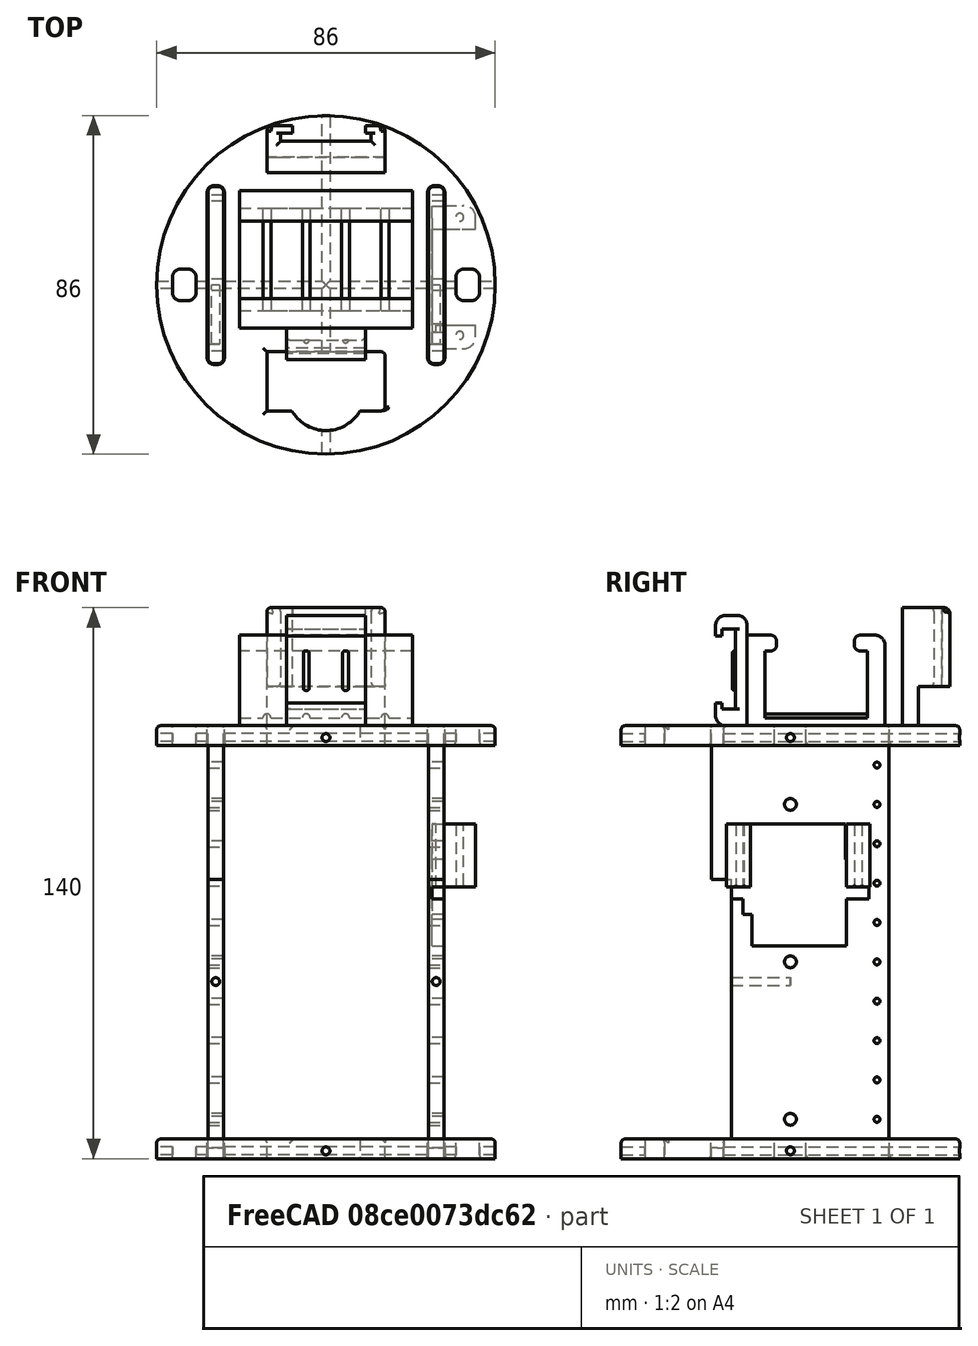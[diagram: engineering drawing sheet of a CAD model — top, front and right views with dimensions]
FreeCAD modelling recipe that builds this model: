
FCSTD DOCUMENT  (FreeCAD 0.20R29603 (Git))
Label: Capsula_Interior
License: All rights reserved
LicenseURL: http://en.wikipedia.org/wiki/All_rights_reserved
objects: Part::Cut×130, Part::Cylinder×98, Part::Fillet×96, Part::Box×72, Part::MultiFuse×37, Part::Offset×12, Part::Chamfer×1
note: 446 computed .brp shape members not serialized (recipe doc carries the construction recipe); baked Part::Feature solids carry a one-line shape summary decoded from their .brp

FEATURE [Part::Box] Box  label="Extensor"
  AttacherType = Attacher::AttachEngine3D
  Height = 66
  Length = 11
  Placement = pos=(30,-28,3) rot=(0,0,1;1.5708rad)
  Width = 60
FEATURE [Part::Box] Box001  label="Cubo001"
  AttacherType = Attacher::AttachEngine3D
  Height = 110
  Length = 45
  Placement = pos=(-30,25,0) rot=(0,0,-1;1.5708rad)
  Width = 4
FEATURE [Part::Box] Box002  label="Cubo002"
  AttacherType = Attacher::AttachEngine3D
  Height = 110
  Length = 45
  Placement = pos=(-30,25,0) rot=(0,0,-1;1.5708rad)
  Width = 4
FEATURE [Part::Box] Box003  label="Cubo003"
  AttacherType = Attacher::AttachEngine3D
  Height = 10
  Length = 30
  Placement = pos=(-15,-32,0) rot=(0,0,1;0rad)
  Width = 15
FEATURE [Part::Box] Box005  label="Cubo004"
  AttacherType = Attacher::AttachEngine3D
  Height = 15
  Length = 26
  Placement = pos=(-13,-23,110) rot=(0,0,1;0rad)
  Width = 35
FEATURE [Part::Box] Box006  label="Cubo005"
  AttacherType = Attacher::AttachEngine3D
  Height = 150
  Length = 6
  Width = 8
FEATURE [Part::Box] Box007  label="Cubo006"
  AttacherType = Attacher::AttachEngine3D
  Height = 150
  Length = 6
  Width = 8
FEATURE [Part::Box] Box008  label="Cubo007"
  AttacherType = Attacher::AttachEngine3D
  Height = 150
  Length = 6
  Width = 8
FEATURE [Part::Box] Box009  label="Cubo008"
  AttacherType = Attacher::AttachEngine3D
  Height = 150
  Length = 6
  Width = 8
FEATURE [Part::Box] Box010  label="Cubo009"
  AttacherType = Attacher::AttachEngine3D
  Height = 11.6
  Length = 20.8
  Placement = pos=(-10.5,-23,110) rot=(0,0,1;0rad)
  Width = 35
FEATURE [Part::Box] Box011  label="Cubo010"
  AttacherType = Attacher::AttachEngine3D
  Height = 11.6
  Length = 16
  Placement = pos=(-8,-23,116) rot=(0,0,1;0rad)
  Width = 35
FEATURE [Part::Box] Box095  label="Cubo095"
  AttacherType = Attacher::AttachEngine3D
  Height = 110
  Length = 45
  Placement = pos=(-30,25,0) rot=(0,0,-1;1.5708rad)
  Width = 4
FEATURE [Part::Box] Box096  label="Cubo096"
  AttacherType = Attacher::AttachEngine3D
  Height = 110
  Length = 45
  Placement = pos=(-30,25,0) rot=(0,0,-1;1.5708rad)
  Width = 4
FEATURE [Part::Box] Box097  label="Cubo097"
  AttacherType = Attacher::AttachEngine3D
  Height = 23
  Length = 24
  Width = 14
FEATURE [Part::Box] Box098  label="Cubo098"
  AttacherType = Attacher::AttachEngine3D
  Height = 3
  Length = 33.5
  Placement = pos=(-5,0,16) rot=(0,0,1;0rad)
  Width = 14
FEATURE [Part::Box] Box099  label="Cubo099"
  AttacherType = Attacher::AttachEngine3D
  Height = 1.4
  Length = 13
  Placement = pos=(9.8,5,28.6) rot=(0,0,1;0rad)
  Width = 4
FEATURE [Part::Box] Box100  label="Cubo100"
  AttacherType = Attacher::AttachEngine3D
  Height = 16
  Length = 10
  Placement = pos=(28,12.2,69) rot=(0,0,1;0rad)
  Width = 6
FEATURE [Part::Box] Box101  label="Cubo101"
  AttacherType = Attacher::AttachEngine3D
  Height = 16
  Length = 10
  Placement = pos=(28,-18.2,69) rot=(0,0,1;0rad)
  Width = 6
FEATURE [Part::Box] Box102  label="Extensor001"
  AttacherType = Attacher::AttachEngine3D
  Height = 66
  Length = 11
  Placement = pos=(30,-28,3) rot=(0,0,1;1.5708rad)
  Width = 60
FEATURE [Part::Box] Box104  label="Cubo102"
  AttacherType = Attacher::AttachEngine3D
  Height = 8
  Length = 20
  Width = 28
FEATURE [Part::Box] Box105  label="Cubo103"
  AttacherType = Attacher::AttachEngine3D
  Height = 2
  Length = 20.5
  Placement = pos=(0,4,4) rot=(0,0,1;0rad)
  Width = 20.5
FEATURE [Part::Box] Box106  label="Cubo104"
  AttacherType = Attacher::AttachEngine3D
  Height = 4
  Length = 20.5
  Placement = pos=(0,5,5) rot=(0,0,1;0rad)
  Width = 18.5
FEATURE [Part::Box] Box107  label="Cubo105"
  AttacherType = Attacher::AttachEngine3D
  Height = 8
  Length = 20
  Width = 30
FEATURE [Part::Box] Box108  label="Cubo106"
  AttacherType = Attacher::AttachEngine3D
  Height = 2
  Length = 20.5
  Placement = pos=(0,3.5,4) rot=(0,0,1;0rad)
  Width = 23
FEATURE [Part::Box] Box109  label="Cubo107"
  AttacherType = Attacher::AttachEngine3D
  Height = 4
  Length = 20.5
  Placement = pos=(0,5,5) rot=(0,0,1;0rad)
  Width = 18.5
FEATURE [Part::Box] Box110  label="Cubo108"
  AttacherType = Attacher::AttachEngine3D
  Height = 10
  Length = 20
  Placement = pos=(-9,-38,105) rot=(0,0,1;0rad)
  Width = 15
FEATURE [Part::Box] Box111  label="Cubo109"
  AttacherType = Attacher::AttachEngine3D
  Height = 110
  Length = 45
  Placement = pos=(-30,25,0) rot=(0,0,-1;1.5708rad)
  Width = 4
FEATURE [Part::Box] Box112  label="Extensor003"
  AttacherType = Attacher::AttachEngine3D
  Height = 66
  Length = 11
  Placement = pos=(30,-28,3) rot=(0,0,1;1.5708rad)
  Width = 60
FEATURE [Part::Box] Box113  label="Extensor004"
  AttacherType = Attacher::AttachEngine3D
  Height = 66
  Length = 11
  Placement = pos=(30,-28,3) rot=(0,0,1;1.5708rad)
  Width = 60
FEATURE [Part::Box] Box114  label="Cubo110"
  AttacherType = Attacher::AttachEngine3D
  Height = 110
  Length = 45
  Placement = pos=(-30,25,0) rot=(0,0,-1;1.5708rad)
  Width = 4
FEATURE [Part::Box] Box115  label="Cubo111"
  AttacherType = Attacher::AttachEngine3D
  Height = 23
  Length = 24
  Width = 14
FEATURE [Part::Box] Box116  label="Cubo112"
  AttacherType = Attacher::AttachEngine3D
  Height = 3
  Length = 33.5
  Placement = pos=(-5,0,16) rot=(0,0,1;0rad)
  Width = 14
FEATURE [Part::Box] Box117  label="Cubo113"
  AttacherType = Attacher::AttachEngine3D
  Height = 1.4
  Length = 13
  Placement = pos=(9.8,5,28.6) rot=(0,0,1;0rad)
  Width = 4
FEATURE [Part::Box] Box118  label="Cubo114"
  AttacherType = Attacher::AttachEngine3D
  Height = 16
  Length = 10
  Placement = pos=(28,12.2,69) rot=(0,0,1;0rad)
  Width = 6
FEATURE [Part::Box] Box119  label="Cubo115"
  AttacherType = Attacher::AttachEngine3D
  Height = 16
  Length = 10
  Placement = pos=(28,-18.2,69) rot=(0,0,1;0rad)
  Width = 6
FEATURE [Part::Box] Box120  label="Cubo116"
  AttacherType = Attacher::AttachEngine3D
  Height = 10
  Length = 4
  Placement = pos=(-30,-20,0) rot=(0,0,1;0rad)
  Width = 45
FEATURE [Part::Box] Box121  label="Cubo117"
  AttacherType = Attacher::AttachEngine3D
  Height = 10
  Length = 4
  Placement = pos=(-30,-20,0) rot=(0,0,1;0rad)
  Width = 45
FEATURE [Part::Box] Box122  label="Cubo118"
  AttacherType = Attacher::AttachEngine3D
  Height = 8
  Length = 20
  Width = 30
FEATURE [Part::Box] Box123  label="Cubo119"
  AttacherType = Attacher::AttachEngine3D
  Height = 2
  Length = 20.5
  Placement = pos=(0,3.5,4) rot=(0,0,1;0rad)
  Width = 23
FEATURE [Part::Box] Box124  label="Cubo120"
  AttacherType = Attacher::AttachEngine3D
  Height = 4
  Length = 20.5
  Placement = pos=(0,5,5) rot=(0,0,1;0rad)
  Width = 18.5
FEATURE [Part::Box] Box128  label="Cubo124"
  AttacherType = Attacher::AttachEngine3D
  Height = 30
  Length = 33
  Placement = pos=(-16,-43,115) rot=(0,0,1;0rad)
  Width = 30
FEATURE [Part::Box] Box129  label="Cubo125"
  AttacherType = Attacher::AttachEngine3D
  Height = 30
  Length = 33
  Placement = pos=(-16,13,110) rot=(0,0,1;0rad)
  Width = 30
FEATURE [Part::Box] Box130  label="Cubo126"
  AttacherType = Attacher::AttachEngine3D
  Height = 30
  Length = 30
  Placement = pos=(-16,13,110) rot=(0,0,1;0rad)
  Width = 4
FEATURE [Part::Box] Box131  label="Cubo127"
  AttacherType = Attacher::AttachEngine3D
  Height = 3.4
  Length = 21
  Placement = pos=(0,4.2,3) rot=(0,0,1;0rad)
  Width = 20.4
FEATURE [Part::Box] Box132  label="Cubo128"
  AttacherType = Attacher::AttachEngine3D
  Height = 4
  Length = 21
  Placement = pos=(0,5.75,6) rot=(0,0,1;0rad)
  Width = 17
FEATURE [Part::Box] Box133  label="Cubo129"
  AttacherType = Attacher::AttachEngine3D
  Height = 8
  Length = 20
  Width = 28
FEATURE [Part::Box] Box134  label="Cubo130"
  AttacherType = Attacher::AttachEngine3D
  Height = 16
  Length = 37
  Placement = pos=(-19,-15,110) rot=(0,0,1;0rad)
  Width = 30
FEATURE [Part::Box] Box135  label="Pila_ext"
  AttacherType = Attacher::AttachEngine3D
  Height = 25
  Length = 44
  Placement = pos=(-22,-11,110) rot=(0,0,1;0rad)
  Width = 35
FEATURE [Part::Box] Box136  label="Pila_int"
  AttacherType = Attacher::AttachEngine3D
  Height = 17
  Length = 44
  Placement = pos=(-22,-6.5,114) rot=(0,0,1;0rad)
  Width = 26
FEATURE [Part::Box] Box137  label="hueco_pila"
  AttacherType = Attacher::AttachEngine3D
  Height = 16.65
  Length = 44
  Placement = pos=(-22,-3.5,122) rot=(0,0,1;0rad)
  Width = 19.72
FEATURE [Part::Box] Box165  label="Cubo155"
  AttacherType = Attacher::AttachEngine3D
  Height = 17
  Length = 19
  Placement = pos=(27,-9.8,59) rot=(0,0,1;0rad)
  Width = 24
FEATURE [Part::Box] Box166  label="Cubo156"
  AttacherType = Attacher::AttachEngine3D
  Height = 66
  Length = 60
  Placement = pos=(-30,-20,5) rot=(0,0,1;0rad)
  Width = 5
FEATURE [Part::Box] Box167  label="Cubo157"
  AttacherType = Attacher::AttachEngine3D
  Height = 66
  Length = 60
  Placement = pos=(-30,-20,5) rot=(0,0,1;0rad)
  Width = 5
FEATURE [Part::Box] Box168  label="Cubo158"
  AttacherType = Attacher::AttachEngine3D
  Height = 3
  Length = 4
  Placement = pos=(27,7,66) rot=(0,0,1;0rad)
  Width = 13
FEATURE [Part::Box] Box169  label="Cubo159"
  AttacherType = Attacher::AttachEngine3D
  Height = 3
  Length = 4
  Placement = pos=(27,-9.8,56) rot=(0,0,1;0rad)
  Width = 24
FEATURE [Part::Box] Box170  label="Cubo160"
  AttacherType = Attacher::AttachEngine3D
  Height = 10
  Length = 30
  Placement = pos=(-15,-32,0) rot=(0,0,1;0rad)
  Width = 15
FEATURE [Part::Box] Box171  label="Cubo161"
  AttacherType = Attacher::AttachEngine3D
  Height = 150
  Length = 6
  Width = 8
FEATURE [Part::Box] Box172  label="Cubo162"
  AttacherType = Attacher::AttachEngine3D
  Height = 150
  Length = 6
  Width = 8
FEATURE [Part::Box] Box173  label="Cubo163"
  AttacherType = Attacher::AttachEngine3D
  Height = 110
  Length = 45
  Placement = pos=(-30,25,0) rot=(0,0,-1;1.5708rad)
  Width = 4
FEATURE [Part::Box] Box174  label="Extensor005"
  AttacherType = Attacher::AttachEngine3D
  Height = 66
  Length = 11
  Placement = pos=(30,-28,3) rot=(0,0,1;1.5708rad)
  Width = 60
FEATURE [Part::Box] Box175  label="Extensor006"
  AttacherType = Attacher::AttachEngine3D
  Height = 66
  Length = 11
  Placement = pos=(30,-28,3) rot=(0,0,1;1.5708rad)
  Width = 60
FEATURE [Part::Box] Box176  label="Cubo164"
  AttacherType = Attacher::AttachEngine3D
  Height = 110
  Length = 45
  Placement = pos=(-30,25,0) rot=(0,0,-1;1.5708rad)
  Width = 4
FEATURE [Part::Box] Box177  label="Cubo165"
  AttacherType = Attacher::AttachEngine3D
  Height = 23
  Length = 24
  Width = 14
FEATURE [Part::Box] Box178  label="Cubo166"
  AttacherType = Attacher::AttachEngine3D
  Height = 3
  Length = 33.5
  Placement = pos=(-5,0,16) rot=(0,0,1;0rad)
  Width = 14
FEATURE [Part::Box] Box179  label="Cubo167"
  AttacherType = Attacher::AttachEngine3D
  Height = 1.4
  Length = 13
  Placement = pos=(9.8,5,28.6) rot=(0,0,1;0rad)
  Width = 4
FEATURE [Part::Box] Box180  label="Cubo168"
  AttacherType = Attacher::AttachEngine3D
  Height = 16
  Length = 10
  Placement = pos=(28,12.2,69) rot=(0,0,1;0rad)
  Width = 6
FEATURE [Part::Box] Box181  label="Cubo169"
  AttacherType = Attacher::AttachEngine3D
  Height = 16
  Length = 10
  Placement = pos=(28,-18.2,69) rot=(0,0,1;0rad)
  Width = 6
FEATURE [Part::Box] Box182  label="Cubo170"
  AttacherType = Attacher::AttachEngine3D
  Height = 10
  Length = 4
  Placement = pos=(-30,-20,0) rot=(0,0,1;0rad)
  Width = 45
FEATURE [Part::Box] Box183  label="Cubo171"
  AttacherType = Attacher::AttachEngine3D
  Height = 10
  Length = 4
  Placement = pos=(-30,-20,0) rot=(0,0,1;0rad)
  Width = 45
FEATURE [Part::Box] Box184  label="Cubo172"
  AttacherType = Attacher::AttachEngine3D
  Height = 10
  Length = 120
  Placement = pos=(-50,-47,100) rot=(0,0,1;0rad)
  Width = 120
FEATURE [Part::Box] Box197  label="Cubo184"
  AttacherType = Attacher::AttachEngine3D
  Height = 16
  Length = 3
  Placement = pos=(27,12,69) rot=(0,0,1;0rad)
  Width = 2
FEATURE [Part::Box] Box198  label="Cubo185"
  AttacherType = Attacher::AttachEngine3D
  Height = 24
  Length = 3
  Placement = pos=(27,14.2,54) rot=(1,0,0;1.5708rad)
  Width = 4
FEATURE [Part::Cut] Cut016
  Base = -> Box005
  Tool = -> Box010
FEATURE [Part::Cut] Cut017
  Base = -> Cut016
  Placement = pos=(-5,0,0) rot=(0,0,1;1.5708rad)
  Tool = -> Box011
FEATURE [Part::Cut] Cut115
  Base = -> Box104
  Tool = -> Box105
FEATURE [Part::Cut] Cut116
  Base = -> Cut115
  Tool = -> Box106
FEATURE [Part::Cut] Cut117
  Base = -> Box107
  Tool = -> Box108
FEATURE [Part::Cut] Cut118
  Base = -> Cut117
  Tool = -> Box109
FEATURE [Part::Cut] Cut143
  Base = -> Box122
  Tool = -> Box123
FEATURE [Part::Cut] Cut144
  Base = -> Cut143
  Tool = -> Box124
FEATURE [Part::Cut] Cut149
  Base = -> Box133
  Tool = -> Box131
FEATURE [Part::Cut] Cut150
  Base = -> Cut149
  Tool = -> Box132
FEATURE [Part::Cut] Cut152
  Base = -> Box135
  Tool = -> Box136
FEATURE [Part::Cut] Cut153  label="PortaPIlas_9V"
  Base = -> Cut152
  Placement = pos=(0,0,-2) rot=(0,0,1;0rad)
  Tool = -> Box137
FEATURE [Part::Cylinder] Cylinder  label="Cilindro"
  Angle = 360
  AttacherType = Attacher::AttachEngine3D
  FirstAngle = 0
  Height = 5
  Radius = 43
  SecondAngle = 0
FEATURE [Part::Cylinder] Cylinder002  label="Cilindro002"
  Angle = 360
  AttacherType = Attacher::AttachEngine3D
  FirstAngle = 0
  Height = 20
  Placement = pos=(0,44,1.5) rot=(1,0,0;1.5708rad)
  Radius = 0.5
  SecondAngle = 0
FEATURE [Part::Cylinder] Cylinder003  label="Cilindro003"
  Angle = 360
  AttacherType = Attacher::AttachEngine3D
  FirstAngle = 0
  Height = 20
  Placement = pos=(0,-26,1.5) rot=(1,0,0;1.5708rad)
  Radius = 0.5
  SecondAngle = 0
FEATURE [Part::Cylinder] Cylinder004  label="Cilindro004"
  Angle = 360
  AttacherType = Attacher::AttachEngine3D
  FirstAngle = 0
  Height = 3
  Radius = 43
  SecondAngle = 0
FEATURE [Part::Cylinder] Cylinder005  label="Cilindro005"
  Angle = 360
  AttacherType = Attacher::AttachEngine3D
  FirstAngle = 0
  Height = 20
  Placement = pos=(0,44,1.5) rot=(1,0,0;1.5708rad)
  Radius = 0.5
  SecondAngle = 0
FEATURE [Part::Cylinder] Cylinder006  label="Cilindro006"
  Angle = 360
  AttacherType = Attacher::AttachEngine3D
  FirstAngle = 0
  Height = 20
  Placement = pos=(0,-26,1.5) rot=(1,0,0;1.5708rad)
  Radius = 0.5
  SecondAngle = 0
FEATURE [Part::Cylinder] Cylinder008  label="Cilindro008"
  Angle = 360
  AttacherType = Attacher::AttachEngine3D
  FirstAngle = 0
  Height = 100
  Placement = pos=(-46,0,50) rot=(0,1,0;1.5708rad)
  Radius = 1.5
  SecondAngle = 0
FEATURE [Part::Cylinder] Cylinder009  label="Cilindro009"
  Angle = 360
  AttacherType = Attacher::AttachEngine3D
  FirstAngle = 0
  Height = 100
  Placement = pos=(-46,0,90) rot=(0,1,0;1.5708rad)
  Radius = 1.5
  SecondAngle = 0
FEATURE [Part::Cylinder] Cylinder010  label="Cilindro010"
  Angle = 360
  AttacherType = Attacher::AttachEngine3D
  FirstAngle = 0
  Height = 100
  Placement = pos=(-46,0,10) rot=(0,1,0;1.5708rad)
  Radius = 1.5
  SecondAngle = 0
FEATURE [Part::Cylinder] Cylinder011  label="Cilindro011"
  Angle = 360
  AttacherType = Attacher::AttachEngine3D
  FirstAngle = 0
  Height = 10
  Placement = pos=(0,-27,0) rot=(0,0,1;0rad)
  Radius = 10
  SecondAngle = 0
FEATURE [Part::Cylinder] Cylinder071  label="Cilindro071"
  Angle = 360
  AttacherType = Attacher::AttachEngine3D
  FirstAngle = 0
  Height = 100
  Placement = pos=(-46,0,50) rot=(0,1,0;1.5708rad)
  Radius = 1.5
  SecondAngle = 0
FEATURE [Part::Cylinder] Cylinder072  label="Cilindro072"
  Angle = 360
  AttacherType = Attacher::AttachEngine3D
  FirstAngle = 0
  Height = 100
  Placement = pos=(-46,0,90) rot=(0,1,0;1.5708rad)
  Radius = 1.5
  SecondAngle = 0
FEATURE [Part::Cylinder] Cylinder073  label="Cilindro073"
  Angle = 360
  AttacherType = Attacher::AttachEngine3D
  FirstAngle = 0
  Height = 100
  Placement = pos=(-46,0,10) rot=(0,1,0;1.5708rad)
  Radius = 1.5
  SecondAngle = 0
FEATURE [Part::Cylinder] Cylinder074  label="Cilindro074"
  Angle = 360
  AttacherType = Attacher::AttachEngine3D
  FirstAngle = 0
  Height = 3
  Placement = pos=(7,7,23) rot=(0,0,1;0rad)
  Radius = 7
  SecondAngle = 0
FEATURE [Part::Cylinder] Cylinder075  label="Cilindro075"
  Angle = 360
  AttacherType = Attacher::AttachEngine3D
  FirstAngle = 0
  Height = 3
  Placement = pos=(14,7,23) rot=(0,0,1;0rad)
  Radius = 2
  SecondAngle = 0
FEATURE [Part::Cylinder] Cylinder076  label="Cilindro076"
  Angle = 360
  AttacherType = Attacher::AttachEngine3D
  FirstAngle = 0
  Height = 10
  Placement = pos=(-3.2,7,12) rot=(0,0,1;0rad)
  Radius = 1.65
  SecondAngle = 0
FEATURE [Part::Cylinder] Cylinder077  label="Cilindro077"
  Angle = 360
  AttacherType = Attacher::AttachEngine3D
  FirstAngle = 0
  Height = 10
  Placement = pos=(26.8,7,12) rot=(0,0,1;0rad)
  Radius = 1.65
  SecondAngle = 0
FEATURE [Part::Cylinder] Cylinder078  label="Cilindro078"
  Angle = 360
  AttacherType = Attacher::AttachEngine3D
  FirstAngle = 0
  Height = 4
  Placement = pos=(7,7,26) rot=(0,0,1;0rad)
  Radius = 3.5
  SecondAngle = 0
FEATURE [Part::Cylinder] Cylinder079  label="Cilindro079"
  Angle = 360
  AttacherType = Attacher::AttachEngine3D
  FirstAngle = 0
  Height = 10
  Placement = pos=(21,7,25) rot=(0,0,1;0rad)
  Radius = 0.25
  SecondAngle = 0
FEATURE [Part::Cylinder] Cylinder080  label="Cilindro080"
  Angle = 360
  AttacherType = Attacher::AttachEngine3D
  FirstAngle = 0
  Height = 10
  Placement = pos=(19,7,25) rot=(0,0,1;0rad)
  Radius = 0.25
  SecondAngle = 0
FEATURE [Part::Cylinder] Cylinder081  label="Cilindro081"
  Angle = 360
  AttacherType = Attacher::AttachEngine3D
  FirstAngle = 0
  Height = 10
  Placement = pos=(17,7,25) rot=(0,0,1;0rad)
  Radius = 0.25
  SecondAngle = 0
FEATURE [Part::Cylinder] Cylinder082  label="Cilindro082"
  Angle = 360
  AttacherType = Attacher::AttachEngine3D
  FirstAngle = 0
  Height = 10
  Placement = pos=(15,7,27) rot=(0,0,1;0rad)
  Radius = 0.25
  SecondAngle = 0
FEATURE [Part::Cylinder] Cylinder083  label="Cilindro083"
  Angle = 360
  AttacherType = Attacher::AttachEngine3D
  FirstAngle = 0
  Height = 10
  Placement = pos=(13,7,27) rot=(0,0,1;0rad)
  Radius = 0.25
  SecondAngle = 0
FEATURE [Part::Cylinder] Cylinder084  label="Cilindro084"
  Angle = 360
  AttacherType = Attacher::AttachEngine3D
  FirstAngle = 0
  Height = 20
  Placement = pos=(34,-14.8,66) rot=(0,0,1;0rad)
  Radius = 1
  SecondAngle = 0
FEATURE [Part::Cylinder] Cylinder085  label="Cilindro085"
  Angle = 360
  AttacherType = Attacher::AttachEngine3D
  FirstAngle = 0
  Height = 20
  Placement = pos=(34,15.2,66) rot=(0,0,1;0rad)
  Radius = 1
  SecondAngle = 0
FEATURE [Part::Cylinder] Cylinder086  label="Cilindro086"
  Angle = 360
  AttacherType = Attacher::AttachEngine3D
  FirstAngle = 0
  Height = 100
  Placement = pos=(-46,0,50) rot=(0,1,0;1.5708rad)
  Radius = 1.5
  SecondAngle = 0
FEATURE [Part::Cylinder] Cylinder087  label="Cilindro087"
  Angle = 360
  AttacherType = Attacher::AttachEngine3D
  FirstAngle = 0
  Height = 100
  Placement = pos=(-46,0,90) rot=(0,1,0;1.5708rad)
  Radius = 1.5
  SecondAngle = 0
FEATURE [Part::Cylinder] Cylinder088  label="Cilindro088"
  Angle = 360
  AttacherType = Attacher::AttachEngine3D
  FirstAngle = 0
  Height = 100
  Placement = pos=(-46,0,10) rot=(0,1,0;1.5708rad)
  Radius = 1.5
  SecondAngle = 0
FEATURE [Part::Cylinder] Cylinder089  label="Cilindro089"
  Angle = 360
  AttacherType = Attacher::AttachEngine3D
  FirstAngle = 0
  Height = 100
  Placement = pos=(-46,0,50) rot=(0,1,0;1.5708rad)
  Radius = 1.5
  SecondAngle = 0
FEATURE [Part::Cylinder] Cylinder090  label="Cilindro090"
  Angle = 360
  AttacherType = Attacher::AttachEngine3D
  FirstAngle = 0
  Height = 100
  Placement = pos=(-46,0,90) rot=(0,1,0;1.5708rad)
  Radius = 1.5
  SecondAngle = 0
FEATURE [Part::Cylinder] Cylinder091  label="Cilindro091"
  Angle = 360
  AttacherType = Attacher::AttachEngine3D
  FirstAngle = 0
  Height = 100
  Placement = pos=(-46,0,10) rot=(0,1,0;1.5708rad)
  Radius = 1.5
  SecondAngle = 0
FEATURE [Part::Cylinder] Cylinder092  label="Cilindro092"
  Angle = 360
  AttacherType = Attacher::AttachEngine3D
  FirstAngle = 0
  Height = 3
  Placement = pos=(7,7,23) rot=(0,0,1;0rad)
  Radius = 7
  SecondAngle = 0
FEATURE [Part::Cylinder] Cylinder093  label="Cilindro093"
  Angle = 360
  AttacherType = Attacher::AttachEngine3D
  FirstAngle = 0
  Height = 3
  Placement = pos=(14,7,23) rot=(0,0,1;0rad)
  Radius = 2
  SecondAngle = 0
FEATURE [Part::Cylinder] Cylinder094  label="Cilindro094"
  Angle = 360
  AttacherType = Attacher::AttachEngine3D
  FirstAngle = 0
  Height = 10
  Placement = pos=(-3.2,7,12) rot=(0,0,1;0rad)
  Radius = 1.65
  SecondAngle = 0
FEATURE [Part::Cylinder] Cylinder095  label="Cilindro095"
  Angle = 360
  AttacherType = Attacher::AttachEngine3D
  FirstAngle = 0
  Height = 10
  Placement = pos=(26.8,7,12) rot=(0,0,1;0rad)
  Radius = 1.65
  SecondAngle = 0
FEATURE [Part::Cylinder] Cylinder096  label="Cilindro096"
  Angle = 360
  AttacherType = Attacher::AttachEngine3D
  FirstAngle = 0
  Height = 4
  Placement = pos=(7,7,26) rot=(0,0,1;0rad)
  Radius = 3.5
  SecondAngle = 0
FEATURE [Part::Cylinder] Cylinder097  label="Cilindro097"
  Angle = 360
  AttacherType = Attacher::AttachEngine3D
  FirstAngle = 0
  Height = 10
  Placement = pos=(21,7,25) rot=(0,0,1;0rad)
  Radius = 0.25
  SecondAngle = 0
FEATURE [Part::Cylinder] Cylinder098  label="Cilindro098"
  Angle = 360
  AttacherType = Attacher::AttachEngine3D
  FirstAngle = 0
  Height = 10
  Placement = pos=(19,7,25) rot=(0,0,1;0rad)
  Radius = 0.25
  SecondAngle = 0
FEATURE [Part::Cylinder] Cylinder099  label="Cilindro099"
  Angle = 360
  AttacherType = Attacher::AttachEngine3D
  FirstAngle = 0
  Height = 10
  Placement = pos=(17,7,25) rot=(0,0,1;0rad)
  Radius = 0.25
  SecondAngle = 0
FEATURE [Part::Cylinder] Cylinder100  label="Cilindro100"
  Angle = 360
  AttacherType = Attacher::AttachEngine3D
  FirstAngle = 0
  Height = 10
  Placement = pos=(15,7,27) rot=(0,0,1;0rad)
  Radius = 0.25
  SecondAngle = 0
FEATURE [Part::Cylinder] Cylinder101  label="Cilindro101"
  Angle = 360
  AttacherType = Attacher::AttachEngine3D
  FirstAngle = 0
  Height = 10
  Placement = pos=(13,7,27) rot=(0,0,1;0rad)
  Radius = 0.25
  SecondAngle = 0
FEATURE [Part::Cylinder] Cylinder102  label="Cilindro102"
  Angle = 360
  AttacherType = Attacher::AttachEngine3D
  FirstAngle = 0
  Height = 20
  Placement = pos=(34,-14.8,66) rot=(0,0,1;0rad)
  Radius = 1
  SecondAngle = 0
FEATURE [Part::Cylinder] Cylinder103  label="Cilindro103"
  Angle = 360
  AttacherType = Attacher::AttachEngine3D
  FirstAngle = 0
  Height = 20
  Placement = pos=(34,15.2,66) rot=(0,0,1;0rad)
  Radius = 1
  SecondAngle = 0
FEATURE [Part::Cylinder] Cylinder104  label="Cilindro104"
  Angle = 360
  AttacherType = Attacher::AttachEngine3D
  FirstAngle = 0
  Height = 100
  Placement = pos=(0,52,2) rot=(1,0,0;1.5708rad)
  Radius = 1
  SecondAngle = 0
FEATURE [Part::Cylinder] Cylinder109  label="Cilindro109"
  Angle = 360
  AttacherType = Attacher::AttachEngine3D
  FirstAngle = 0
  Height = 15
  Placement = pos=(-28,0,45) rot=(1,0,0;1.5708rad)
  Radius = 1
  SecondAngle = 0
FEATURE [Part::Cylinder] Cylinder110  label="Cilindro110"
  Angle = 360
  AttacherType = Attacher::AttachEngine3D
  FirstAngle = 0
  Height = 15
  Placement = pos=(28,0,45) rot=(1,0,0;1.5708rad)
  Radius = 1
  SecondAngle = 0
FEATURE [Part::Cylinder] Cylinder111  label="Cilindro111"
  Angle = 360
  AttacherType = Attacher::AttachEngine3D
  FirstAngle = 0
  Height = 67
  Placement = pos=(-33,22,10) rot=(0,1,0;1.5708rad)
  Radius = 0.75
  SecondAngle = 0
FEATURE [Part::Cylinder] Cylinder112  label="Cilindro112"
  Angle = 360
  AttacherType = Attacher::AttachEngine3D
  FirstAngle = 0
  Height = 67
  Placement = pos=(-33,22,100) rot=(0,1,0;1.5708rad)
  Radius = 0.75
  SecondAngle = 0
FEATURE [Part::Cylinder] Cylinder113  label="Cilindro113"
  Angle = 360
  AttacherType = Attacher::AttachEngine3D
  FirstAngle = 0
  Height = 67
  Placement = pos=(-33,22,20) rot=(0,1,0;1.5708rad)
  Radius = 0.75
  SecondAngle = 0
FEATURE [Part::Cylinder] Cylinder114  label="Cilindro114"
  Angle = 360
  AttacherType = Attacher::AttachEngine3D
  FirstAngle = 0
  Height = 67
  Placement = pos=(-33,22,30) rot=(0,1,0;1.5708rad)
  Radius = 0.75
  SecondAngle = 0
FEATURE [Part::Cylinder] Cylinder115  label="Cilindro115"
  Angle = 360
  AttacherType = Attacher::AttachEngine3D
  FirstAngle = 0
  Height = 67
  Placement = pos=(-33,22,40) rot=(0,1,0;1.5708rad)
  Radius = 0.75
  SecondAngle = 0
FEATURE [Part::Cylinder] Cylinder116  label="Cilindro116"
  Angle = 360
  AttacherType = Attacher::AttachEngine3D
  FirstAngle = 0
  Height = 67
  Placement = pos=(-33,22,50) rot=(0,1,0;1.5708rad)
  Radius = 0.75
  SecondAngle = 0
FEATURE [Part::Cylinder] Cylinder117  label="Cilindro117"
  Angle = 360
  AttacherType = Attacher::AttachEngine3D
  FirstAngle = 0
  Height = 67
  Placement = pos=(-33,22,60) rot=(0,1,0;1.5708rad)
  Radius = 0.75
  SecondAngle = 0
FEATURE [Part::Cylinder] Cylinder118  label="Cilindro118"
  Angle = 360
  AttacherType = Attacher::AttachEngine3D
  FirstAngle = 0
  Height = 67
  Placement = pos=(-33,22,70) rot=(0,1,0;1.5708rad)
  Radius = 0.75
  SecondAngle = 0
FEATURE [Part::Cylinder] Cylinder119  label="Cilindro119"
  Angle = 360
  AttacherType = Attacher::AttachEngine3D
  FirstAngle = 0
  Height = 67
  Placement = pos=(-33,22,80) rot=(0,1,0;1.5708rad)
  Radius = 0.75
  SecondAngle = 0
FEATURE [Part::Cylinder] Cylinder120  label="Cilindro120"
  Angle = 360
  AttacherType = Attacher::AttachEngine3D
  FirstAngle = 0
  Height = 67
  Placement = pos=(-33,22,90) rot=(0,1,0;1.5708rad)
  Radius = 0.75
  SecondAngle = 0
FEATURE [Part::Cylinder] Cylinder121  label="Cilindro121"
  Angle = 360
  AttacherType = Attacher::AttachEngine3D
  FirstAngle = 0
  Height = 67
  Placement = pos=(-33,22,10) rot=(0,1,0;1.5708rad)
  Radius = 0.75
  SecondAngle = 0
FEATURE [Part::Cylinder] Cylinder122  label="Cilindro122"
  Angle = 360
  AttacherType = Attacher::AttachEngine3D
  FirstAngle = 0
  Height = 67
  Placement = pos=(-33,22,100) rot=(0,1,0;1.5708rad)
  Radius = 0.75
  SecondAngle = 0
FEATURE [Part::Cylinder] Cylinder123  label="Cilindro123"
  Angle = 360
  AttacherType = Attacher::AttachEngine3D
  FirstAngle = 0
  Height = 67
  Placement = pos=(-33,22,20) rot=(0,1,0;1.5708rad)
  Radius = 0.75
  SecondAngle = 0
FEATURE [Part::Cylinder] Cylinder124  label="Cilindro124"
  Angle = 360
  AttacherType = Attacher::AttachEngine3D
  FirstAngle = 0
  Height = 67
  Placement = pos=(-33,22,30) rot=(0,1,0;1.5708rad)
  Radius = 0.75
  SecondAngle = 0
FEATURE [Part::Cylinder] Cylinder125  label="Cilindro125"
  Angle = 360
  AttacherType = Attacher::AttachEngine3D
  FirstAngle = 0
  Height = 67
  Placement = pos=(-33,22,40) rot=(0,1,0;1.5708rad)
  Radius = 0.75
  SecondAngle = 0
FEATURE [Part::Cylinder] Cylinder126  label="Cilindro126"
  Angle = 360
  AttacherType = Attacher::AttachEngine3D
  FirstAngle = 0
  Height = 67
  Placement = pos=(-33,22,50) rot=(0,1,0;1.5708rad)
  Radius = 0.75
  SecondAngle = 0
FEATURE [Part::Cylinder] Cylinder127  label="Cilindro127"
  Angle = 360
  AttacherType = Attacher::AttachEngine3D
  FirstAngle = 0
  Height = 67
  Placement = pos=(-33,22,60) rot=(0,1,0;1.5708rad)
  Radius = 0.75
  SecondAngle = 0
FEATURE [Part::Cylinder] Cylinder128  label="Cilindro128"
  Angle = 360
  AttacherType = Attacher::AttachEngine3D
  FirstAngle = 0
  Height = 67
  Placement = pos=(-33,22,70) rot=(0,1,0;1.5708rad)
  Radius = 0.75
  SecondAngle = 0
FEATURE [Part::Cylinder] Cylinder129  label="Cilindro129"
  Angle = 360
  AttacherType = Attacher::AttachEngine3D
  FirstAngle = 0
  Height = 67
  Placement = pos=(-33,22,80) rot=(0,1,0;1.5708rad)
  Radius = 0.75
  SecondAngle = 0
FEATURE [Part::Cylinder] Cylinder130  label="Cilindro130"
  Angle = 360
  AttacherType = Attacher::AttachEngine3D
  FirstAngle = 0
  Height = 67
  Placement = pos=(-33,22,90) rot=(0,1,0;1.5708rad)
  Radius = 0.75
  SecondAngle = 0
FEATURE [Part::Cylinder] Cylinder131  label="Cilindro131"
  Angle = 360
  AttacherType = Attacher::AttachEngine3D
  FirstAngle = 0
  Height = 67
  Placement = pos=(-33,22,70) rot=(0,1,0;1.5708rad)
  Radius = 0.75
  SecondAngle = 0
FEATURE [Part::Cylinder] Cylinder133  label="Cilindro133"
  Angle = 360
  AttacherType = Attacher::AttachEngine3D
  FirstAngle = 0
  Height = 110
  Placement = pos=(-55,0,2) rot=(0.57735,0.57735,0.57735;2.0944rad)
  Radius = 1
  SecondAngle = 0
FEATURE [Part::Cylinder] Cylinder134  label="Cilindro134"
  Angle = 360
  AttacherType = Attacher::AttachEngine3D
  FirstAngle = 0
  Height = 5
  Radius = 43
  SecondAngle = 0
FEATURE [Part::Cylinder] Cylinder135  label="Cilindro135"
  Angle = 360
  AttacherType = Attacher::AttachEngine3D
  FirstAngle = 0
  Height = 20
  Placement = pos=(0,44,1.5) rot=(1,0,0;1.5708rad)
  Radius = 0.5
  SecondAngle = 0
FEATURE [Part::Cylinder] Cylinder136  label="Cilindro136"
  Angle = 360
  AttacherType = Attacher::AttachEngine3D
  FirstAngle = 0
  Height = 20
  Placement = pos=(0,-26,1.5) rot=(1,0,0;1.5708rad)
  Radius = 0.5
  SecondAngle = 0
FEATURE [Part::Cylinder] Cylinder137  label="Cilindro137"
  Angle = 360
  AttacherType = Attacher::AttachEngine3D
  FirstAngle = 0
  Height = 10
  Placement = pos=(0,-27,0) rot=(0,0,1;0rad)
  Radius = 10
  SecondAngle = 0
FEATURE [Part::Cylinder] Cylinder138  label="Cilindro138"
  Angle = 360
  AttacherType = Attacher::AttachEngine3D
  FirstAngle = 0
  Height = 100
  Placement = pos=(-46,0,50) rot=(0,1,0;1.5708rad)
  Radius = 1.5
  SecondAngle = 0
FEATURE [Part::Cylinder] Cylinder139  label="Cilindro139"
  Angle = 360
  AttacherType = Attacher::AttachEngine3D
  FirstAngle = 0
  Height = 100
  Placement = pos=(-46,0,90) rot=(0,1,0;1.5708rad)
  Radius = 1.5
  SecondAngle = 0
FEATURE [Part::Cylinder] Cylinder140  label="Cilindro140"
  Angle = 360
  AttacherType = Attacher::AttachEngine3D
  FirstAngle = 0
  Height = 100
  Placement = pos=(-46,0,10) rot=(0,1,0;1.5708rad)
  Radius = 1.5
  SecondAngle = 0
FEATURE [Part::Cylinder] Cylinder141  label="Cilindro141"
  Angle = 360
  AttacherType = Attacher::AttachEngine3D
  FirstAngle = 0
  Height = 100
  Placement = pos=(-46,0,50) rot=(0,1,0;1.5708rad)
  Radius = 1.5
  SecondAngle = 0
FEATURE [Part::Cylinder] Cylinder142  label="Cilindro142"
  Angle = 360
  AttacherType = Attacher::AttachEngine3D
  FirstAngle = 0
  Height = 100
  Placement = pos=(-46,0,90) rot=(0,1,0;1.5708rad)
  Radius = 1.5
  SecondAngle = 0
FEATURE [Part::Cylinder] Cylinder143  label="Cilindro143"
  Angle = 360
  AttacherType = Attacher::AttachEngine3D
  FirstAngle = 0
  Height = 100
  Placement = pos=(-46,0,10) rot=(0,1,0;1.5708rad)
  Radius = 1.5
  SecondAngle = 0
FEATURE [Part::Cylinder] Cylinder144  label="Cilindro144"
  Angle = 360
  AttacherType = Attacher::AttachEngine3D
  FirstAngle = 0
  Height = 3
  Placement = pos=(7,7,23) rot=(0,0,1;0rad)
  Radius = 7
  SecondAngle = 0
FEATURE [Part::Cylinder] Cylinder145  label="Cilindro145"
  Angle = 360
  AttacherType = Attacher::AttachEngine3D
  FirstAngle = 0
  Height = 3
  Placement = pos=(14,7,23) rot=(0,0,1;0rad)
  Radius = 2
  SecondAngle = 0
FEATURE [Part::Cylinder] Cylinder146  label="Cilindro146"
  Angle = 360
  AttacherType = Attacher::AttachEngine3D
  FirstAngle = 0
  Height = 10
  Placement = pos=(-3.2,7,12) rot=(0,0,1;0rad)
  Radius = 1.65
  SecondAngle = 0
FEATURE [Part::Cylinder] Cylinder147  label="Cilindro147"
  Angle = 360
  AttacherType = Attacher::AttachEngine3D
  FirstAngle = 0
  Height = 10
  Placement = pos=(26.8,7,12) rot=(0,0,1;0rad)
  Radius = 1.65
  SecondAngle = 0
FEATURE [Part::Cylinder] Cylinder148  label="Cilindro148"
  Angle = 360
  AttacherType = Attacher::AttachEngine3D
  FirstAngle = 0
  Height = 4
  Placement = pos=(7,7,26) rot=(0,0,1;0rad)
  Radius = 3.5
  SecondAngle = 0
FEATURE [Part::Cylinder] Cylinder149  label="Cilindro149"
  Angle = 360
  AttacherType = Attacher::AttachEngine3D
  FirstAngle = 0
  Height = 10
  Placement = pos=(21,7,25) rot=(0,0,1;0rad)
  Radius = 0.25
  SecondAngle = 0
FEATURE [Part::Cylinder] Cylinder150  label="Cilindro150"
  Angle = 360
  AttacherType = Attacher::AttachEngine3D
  FirstAngle = 0
  Height = 10
  Placement = pos=(19,7,25) rot=(0,0,1;0rad)
  Radius = 0.25
  SecondAngle = 0
FEATURE [Part::Cylinder] Cylinder151  label="Cilindro151"
  Angle = 360
  AttacherType = Attacher::AttachEngine3D
  FirstAngle = 0
  Height = 10
  Placement = pos=(17,7,25) rot=(0,0,1;0rad)
  Radius = 0.25
  SecondAngle = 0
FEATURE [Part::Cylinder] Cylinder152  label="Cilindro152"
  Angle = 360
  AttacherType = Attacher::AttachEngine3D
  FirstAngle = 0
  Height = 10
  Placement = pos=(15,7,27) rot=(0,0,1;0rad)
  Radius = 0.25
  SecondAngle = 0
FEATURE [Part::Cylinder] Cylinder153  label="Cilindro153"
  Angle = 360
  AttacherType = Attacher::AttachEngine3D
  FirstAngle = 0
  Height = 10
  Placement = pos=(13,7,27) rot=(0,0,1;0rad)
  Radius = 0.25
  SecondAngle = 0
FEATURE [Part::Cylinder] Cylinder154  label="Cilindro154"
  Angle = 360
  AttacherType = Attacher::AttachEngine3D
  FirstAngle = 0
  Height = 20
  Placement = pos=(34,-14.8,66) rot=(0,0,1;0rad)
  Radius = 1
  SecondAngle = 0
FEATURE [Part::Cylinder] Cylinder155  label="Cilindro155"
  Angle = 360
  AttacherType = Attacher::AttachEngine3D
  FirstAngle = 0
  Height = 20
  Placement = pos=(34,15.2,66) rot=(0,0,1;0rad)
  Radius = 1
  SecondAngle = 0
FEATURE [Part::Cylinder] Cylinder156  label="Cilindro156"
  Angle = 360
  AttacherType = Attacher::AttachEngine3D
  FirstAngle = 0
  Height = 100
  Placement = pos=(0,52,2) rot=(1,0,0;1.5708rad)
  Radius = 1
  SecondAngle = 0
FEATURE [Part::Cylinder] Cylinder157  label="Cilindro157"
  Angle = 360
  AttacherType = Attacher::AttachEngine3D
  FirstAngle = 0
  Height = 110
  Placement = pos=(-55,0,2) rot=(0.57735,0.57735,0.57735;2.0944rad)
  Radius = 1
  SecondAngle = 0
FEATURE [Part::Cylinder] Cylinder158  label="Cilindro158"
  Angle = 360
  AttacherType = Attacher::AttachEngine3D
  FirstAngle = 0
  Height = 29
  Placement = pos=(-15,22,112) rot=(1,0,0;1.5708rad)
  Radius = 1
  SecondAngle = 0
FEATURE [Part::Cylinder] Cylinder159  label="Cilindro159"
  Angle = 360
  AttacherType = Attacher::AttachEngine3D
  FirstAngle = 0
  Height = 29
  Placement = pos=(-5,22,112) rot=(1,0,0;1.5708rad)
  Radius = 1
  SecondAngle = 0
FEATURE [Part::Cylinder] Cylinder160  label="Cilindro160"
  Angle = 360
  AttacherType = Attacher::AttachEngine3D
  FirstAngle = 0
  Height = 29
  Placement = pos=(5,22,112) rot=(1,0,0;1.5708rad)
  Radius = 1
  SecondAngle = 0
FEATURE [Part::Cylinder] Cylinder161  label="Cilindro161"
  Angle = 360
  AttacherType = Attacher::AttachEngine3D
  FirstAngle = 0
  Height = 29
  Placement = pos=(15,22,112) rot=(1,0,0;1.5708rad)
  Radius = 1
  SecondAngle = 0
FEATURE [Part::Cylinder] Cylinder162  label="Cilindro162"
  Angle = 360
  AttacherType = Attacher::AttachEngine3D
  FirstAngle = 0
  Height = 10
  Placement = pos=(-5,-14,119) rot=(0,0,1;0rad)
  Radius = 0.75
  SecondAngle = 0
FEATURE [Part::Cylinder] Cylinder163  label="Cilindro163"
  Angle = 360
  AttacherType = Attacher::AttachEngine3D
  FirstAngle = 0
  Height = 10
  Placement = pos=(5,-14,119) rot=(0,0,1;0rad)
  Radius = 0.75
  SecondAngle = 0
FEATURE [Part::Fillet] Fillet
  Base = -> Cylinder
  Edges = 1 edges r=1: [Edge3]
FEATURE [Part::Cut] Cut
  Base = -> Fillet
  Tool = -> Cylinder003
FEATURE [Part::Cut] Cut001  label="BaseInf"
  Base = -> Cut
  Tool = -> Cylinder002
FEATURE [Part::Cut] Cut093  label="BaseInf001"
  Base = -> Cut001
  Tool = -> Cylinder011
FEATURE [Part::Cut] Cut094  label="BaseInf002"
  Base = -> Cut093
  Tool = -> Box003
FEATURE [Part::Fillet] Fillet003
  Base = -> Cut118
  Edges = 1 edges r=1: [Edge23]
FEATURE [Part::Fillet] Fillet004
  Base = -> Fillet003
  Edges = 1 edges r=1: [Edge4]
FEATURE [Part::Fillet] Fillet005  label="PortaSensor_Inclinacion001"
  Base = -> Fillet004
  Edges = 1 edges r=1: [Edge34]
  Placement = pos=(0,3.5,4) rot=(0,0,1;0rad)
FEATURE [Part::Fillet] Fillet006
  Base = -> Fillet005
  Edges = 1 edges r=1: [Edge48]
FEATURE [Part::Fillet] Fillet007  label="PortaSensor_TemHum"
  Base = -> Fillet006
  Edges = 2 edges r=1: [Edge7,Edge18]
  Placement = pos=(-18,-9,137) rot=(0.57735,0.57735,-0.57735;2.0944rad)
FEATURE [Part::Fillet] Fillet009
  Base = -> Cylinder004
  Edges = 1 edges r=1: [Edge3]
FEATURE [Part::Cut] Cut002
  Base = -> Fillet009
  Tool = -> Cylinder006
FEATURE [Part::Cut] Cut003
  Base = -> Cut002
  Placement = pos=(0,0,97) rot=(0,0,1;0rad)
  Tool = -> Cylinder005
FEATURE [Part::Fillet] Fillet010
  Base = -> Box001
  Edges = 2 edges r=1.5: [Edge1,Edge3]
FEATURE [Part::Fillet] Fillet011  label="Lateral_Iz"
  Base = -> Fillet010
  Edges = 2 edges r=1.5: [Edge17,Edge18]
FEATURE [Part::Fillet] Fillet012
  Base = -> Box002
  Edges = 2 edges r=1.5: [Edge1,Edge3]
FEATURE [Part::Fillet] Fillet013  label="Lateral_De"
  Base = -> Fillet012
  Edges = 2 edges r=1.5: [Edge17,Edge18]
  Placement = pos=(56,0,0) rot=(0,0,1;0rad)
FEATURE [Part::Fillet] Fillet019
  Base = -> Box006
  Edges = 4 edges r=2: [Edge1,Edge3,Edge5,Edge7]
  Placement = pos=(-39,-4,0) rot=(0,0,1;0rad)
FEATURE [Part::Fillet] Fillet020
  Base = -> Box007
  Edges = 4 edges r=2: [Edge1,Edge3,Edge5,Edge7]
  Placement = pos=(33,-4,0) rot=(0,0,1;0rad)
FEATURE [Part::Fillet] Fillet021
  Base = -> Box008
  Edges = 4 edges r=2: [Edge1,Edge3,Edge5,Edge7]
  Placement = pos=(-39,-4,0) rot=(0,0,1;0rad)
FEATURE [Part::Cut] Cut095
  Base = -> Cut094
  Tool = -> Fillet021
FEATURE [Part::Cut] Cut096  label="BaseInf003"
  Base = -> Cut095
  Tool = -> Fillet020
FEATURE [Part::Fillet] Fillet022
  Base = -> Box009
  Edges = 4 edges r=2: [Edge1,Edge3,Edge5,Edge7]
  Placement = pos=(33,-4,0) rot=(0,0,1;0rad)
FEATURE [Part::Fillet] Fillet032
  Base = -> Box095
  Edges = 2 edges r=1.5: [Edge1,Edge3]
FEATURE [Part::Fillet] Fillet033  label="Lateral_De001"
  Base = -> Fillet032
  Edges = 2 edges r=1.5: [Edge17,Edge18]
  Placement = pos=(56,0,0) rot=(0,0,1;0rad)
FEATURE [Part::Cut] Cut100
  Base = -> Fillet033
  Tool = -> Cylinder010
FEATURE [Part::Cut] Cut101
  Base = -> Cut100
  Tool = -> Cylinder009
FEATURE [Part::Cut] Cut102
  Base = -> Cut101
  Tool = -> Cylinder008
FEATURE [Part::Fillet] Fillet034
  Base = -> Box096
  Edges = 2 edges r=1.5: [Edge1,Edge3]
FEATURE [Part::Fillet] Fillet035  label="Lateral_Iz001"
  Base = -> Fillet034
  Edges = 2 edges r=1.5: [Edge17,Edge18]
FEATURE [Part::Cut] Cut097
  Base = -> Fillet035
  Tool = -> Cylinder071
FEATURE [Part::Cut] Cut098
  Base = -> Cut097
  Tool = -> Cylinder073
FEATURE [Part::Cut] Cut099  label="Lateral_Iz002"
  Base = -> Cut098
  Tool = -> Cylinder072
FEATURE [Part::Fillet] Fillet039
  Base = -> Box100
  Edges = 1 edges r=3: [Edge7]
FEATURE [Part::Cut] Cut112
  Base = -> Fillet039
  Tool = -> Cylinder085
FEATURE [Part::Fillet] Fillet040
  Base = -> Box101
  Edges = 1 edges r=3: [Edge5]
FEATURE [Part::Cut] Cut111
  Base = -> Fillet040
  Tool = -> Cylinder084
FEATURE [Part::Fillet] Fillet041
  Base = -> Cut111
  Edges = 1 edges r=0.5: [Edge15]
  Placement = pos=(0,2,0) rot=(0,0,1;0rad)
FEATURE [Part::Fillet] Fillet042
  Base = -> Cut112
  Edges = 1 edges r=0.5: [Edge15]
  Placement = pos=(0,2,0) rot=(0,0,1;0rad)
FEATURE [Part::Fillet] Fillet043
  Base = -> Cut116
  Edges = 1 edges r=1: [Edge23]
FEATURE [Part::Fillet] Fillet001
  Base = -> Fillet043
  Edges = 1 edges r=1: [Edge4]
FEATURE [Part::Fillet] Fillet002  label="PortaSensor"
  Base = -> Fillet001
  Edges = 1 edges r=1: [Edge34]
  Placement = pos=(-12,11,110) rot=(0,0,1;0rad)
FEATURE [Part::Fillet] Fillet044
  Base = -> Fillet002
  Edges = 1 edges r=1: [Edge48]
FEATURE [Part::Fillet] Fillet045
  Base = -> Fillet044
  Edges = 1 edges r=1: [Edge18]
FEATURE [Part::Fillet] Fillet046
  Base = -> Fillet045
  Edges = 1 edges r=1: [Edge22]
FEATURE [Part::Fillet] Fillet049
  Base = -> Box110
  Edges = 4 edges r=6: [Edge1,Edge3,Edge5,Edge7]
FEATURE [Part::Fillet] Fillet051
  Base = -> Box111
  Edges = 2 edges r=1.5: [Edge1,Edge3]
FEATURE [Part::Fillet] Fillet052  label="Lateral_Iz006"
  Base = -> Fillet051
  Edges = 2 edges r=1.5: [Edge17,Edge18]
FEATURE [Part::Cut] Cut120
  Base = -> Fillet052
  Tool = -> Cylinder086
FEATURE [Part::Cut] Cut121
  Base = -> Cut120
  Tool = -> Cylinder088
FEATURE [Part::Cut] Cut122  label="Lateral_Iz004"
  Base = -> Cut121
  Tool = -> Cylinder087
FEATURE [Part::Fillet] Fillet053
  Base = -> Box114
  Edges = 2 edges r=1.5: [Edge1,Edge3]
FEATURE [Part::Fillet] Fillet054  label="Lateral_De005"
  Base = -> Fillet053
  Edges = 2 edges r=1.5: [Edge17,Edge18]
  Placement = pos=(56,0,0) rot=(0,0,1;0rad)
FEATURE [Part::Cut] Cut124
  Base = -> Fillet054
  Tool = -> Cylinder091
FEATURE [Part::Cut] Cut125
  Base = -> Cut124
  Tool = -> Cylinder090
FEATURE [Part::Cut] Cut126
  Base = -> Cut125
  Tool = -> Cylinder089
FEATURE [Part::Fillet] Fillet058
  Base = -> Box118
  Edges = 1 edges r=3: [Edge7]
FEATURE [Part::Cut] Cut136
  Base = -> Fillet058
  Tool = -> Cylinder103
FEATURE [Part::Fillet] Fillet059
  Base = -> Box119
  Edges = 1 edges r=3: [Edge5]
FEATURE [Part::Cut] Cut135
  Base = -> Fillet059
  Tool = -> Cylinder102
FEATURE [Part::Fillet] Fillet060
  Base = -> Cut135
  Edges = 1 edges r=0.5: [Edge15]
  Placement = pos=(0,2,0) rot=(0,0,1;0rad)
FEATURE [Part::Fillet] Fillet061
  Base = -> Cut136
  Edges = 1 edges r=0.5: [Edge15]
  Placement = pos=(0,2,0) rot=(0,0,1;0rad)
FEATURE [Part::Fillet] Fillet062
  Base = -> Box120
  Edges = 2 edges r=1.5: [Edge3,Edge7]
FEATURE [Part::Fillet] Fillet063
  Base = -> Fillet062
  Edges = 2 edges r=1.5: [Edge2,Edge13]
  Placement = pos=(0,0,-3) rot=(0,0,1;0rad)
FEATURE [Part::Fillet] Fillet064
  Base = -> Box121
  Edges = 2 edges r=1.5: [Edge3,Edge7]
FEATURE [Part::Fillet] Fillet065
  Base = -> Fillet064
  Edges = 2 edges r=1.5: [Edge2,Edge13]
  Placement = pos=(0,0,-3) rot=(0,0,1;0rad)
FEATURE [Part::Fillet] Fillet069
  Base = -> Cut144
  Edges = 1 edges r=1: [Edge23]
FEATURE [Part::Fillet] Fillet070
  Base = -> Fillet069
  Edges = 1 edges r=1: [Edge4]
FEATURE [Part::Fillet] Fillet071  label="PortaSensor_Inclinacion002"
  Base = -> Fillet070
  Edges = 1 edges r=1: [Edge34]
  Placement = pos=(0,3.5,4) rot=(0,0,1;0rad)
FEATURE [Part::Fillet] Fillet072
  Base = -> Fillet071
  Edges = 1 edges r=1: [Edge48]
FEATURE [Part::Fillet] Fillet073  label="PortaSensor_TemHum001"
  Base = -> Fillet072
  Edges = 2 edges r=1: [Edge7,Edge18]
  Placement = pos=(17.5,13,140) rot=(0.57735,-0.57735,-0.57735;4.18879rad)
FEATURE [Part::Fillet] Fillet081
  Base = -> Cut150
  Edges = 1 edges r=1: [Edge23]
FEATURE [Part::Fillet] Fillet082  label="PortaSensor_Inclinación"
  Base = -> Fillet081
  Edges = 1 edges r=1: [Edge8]
  Placement = pos=(-10,-11,110) rot=(1,0,0;1.5708rad)
FEATURE [Part::Fillet] Fillet083
  Base = -> Cut153
  Edges = 2 edges r=1.5: [Edge13,Edge29]
FEATURE [Part::Fillet] Fillet084  label="PortaPilas_9V"
  Base = -> Fillet083
  Edges = 2 edges r=1.5: [Edge23,Edge41]
FEATURE [Part::Fillet] Fillet120
  Base = -> Cylinder134
  Edges = 1 edges r=1: [Edge3]
FEATURE [Part::Cut] Cut205
  Base = -> Fillet120
  Tool = -> Cylinder136
FEATURE [Part::Cut] Cut206  label="BaseInf010"
  Base = -> Cut205
  Tool = -> Cylinder135
FEATURE [Part::Cut] Cut207  label="BaseInf011"
  Base = -> Cut206
  Tool = -> Cylinder137
FEATURE [Part::Cut] Cut208  label="BaseInf012"
  Base = -> Cut207
  Tool = -> Box170
FEATURE [Part::Fillet] Fillet121
  Base = -> Box171
  Edges = 4 edges r=2: [Edge1,Edge3,Edge5,Edge7]
  Placement = pos=(33,-4,0) rot=(0,0,1;0rad)
FEATURE [Part::Fillet] Fillet122
  Base = -> Box172
  Edges = 4 edges r=2: [Edge1,Edge3,Edge5,Edge7]
  Placement = pos=(-39,-4,0) rot=(0,0,1;0rad)
FEATURE [Part::Cut] Cut209
  Base = -> Cut208
  Tool = -> Fillet122
FEATURE [Part::Cut] Cut210  label="BaseInf013"
  Base = -> Cut209
  Tool = -> Fillet121
FEATURE [Part::Fillet] Fillet123
  Base = -> Box173
  Edges = 2 edges r=1.5: [Edge1,Edge3]
FEATURE [Part::Fillet] Fillet124  label="Lateral_Iz010"
  Base = -> Fillet123
  Edges = 2 edges r=1.5: [Edge17,Edge18]
FEATURE [Part::Cut] Cut211
  Base = -> Fillet124
  Tool = -> Cylinder138
FEATURE [Part::Cut] Cut212
  Base = -> Cut211
  Tool = -> Cylinder140
FEATURE [Part::Cut] Cut213  label="Lateral_Iz008"
  Base = -> Cut212
  Tool = -> Cylinder139
FEATURE [Part::Fillet] Fillet125
  Base = -> Box176
  Edges = 2 edges r=1.5: [Edge1,Edge3]
FEATURE [Part::Fillet] Fillet126  label="Lateral_De009"
  Base = -> Fillet125
  Edges = 2 edges r=1.5: [Edge17,Edge18]
  Placement = pos=(56,0,0) rot=(0,0,1;0rad)
FEATURE [Part::Cut] Cut215
  Base = -> Fillet126
  Tool = -> Cylinder143
FEATURE [Part::Cut] Cut216
  Base = -> Cut215
  Tool = -> Cylinder142
FEATURE [Part::Cut] Cut217
  Base = -> Cut216
  Tool = -> Cylinder141
FEATURE [Part::Fillet] Fillet130
  Base = -> Box180
  Edges = 1 edges r=3: [Edge7]
FEATURE [Part::Cut] Cut227
  Base = -> Fillet130
  Tool = -> Cylinder155
FEATURE [Part::Fillet] Fillet131
  Base = -> Box181
  Edges = 1 edges r=3: [Edge5]
FEATURE [Part::Cut] Cut226
  Base = -> Fillet131
  Tool = -> Cylinder154
FEATURE [Part::Fillet] Fillet132
  Base = -> Cut226
  Edges = 1 edges r=0.5: [Edge15]
  Placement = pos=(0,2,0) rot=(0,0,1;0rad)
FEATURE [Part::Fillet] Fillet133
  Base = -> Cut227
  Edges = 1 edges r=0.5: [Edge15]
  Placement = pos=(0,2,0) rot=(0,0,1;0rad)
FEATURE [Part::Fillet] Fillet134
  Base = -> Box182
  Edges = 2 edges r=1.5: [Edge3,Edge7]
FEATURE [Part::Fillet] Fillet135
  Base = -> Fillet134
  Edges = 2 edges r=1.5: [Edge2,Edge13]
  Placement = pos=(0,0,-3) rot=(0,0,1;0rad)
FEATURE [Part::Fillet] Fillet136
  Base = -> Box183
  Edges = 2 edges r=1.5: [Edge3,Edge7]
FEATURE [Part::Fillet] Fillet137
  Base = -> Fillet136
  Edges = 2 edges r=1.5: [Edge2,Edge13]
  Placement = pos=(0,0,-3) rot=(0,0,1;0rad)
FEATURE [Part::Fillet] Fillet145
  Base = -> Cylinder162
  Edges = 1 edges r=0.5: [Edge3]
FEATURE [Part::Fillet] Fillet146
  Base = -> Fillet145
  Edges = 1 edges r=0.5: [Edge3]
FEATURE [Part::Fillet] Fillet147
  Base = -> Cylinder163
  Edges = 1 edges r=0.5: [Edge3]
FEATURE [Part::Fillet] Fillet148
  Base = -> Fillet147
  Edges = 1 edges r=0.5: [Edge3]
FEATURE [Part::MultiFuse] Fusion069
  Shapes = -> [Cylinder074,Cylinder075]
FEATURE [Part::MultiFuse] Fusion070
  Shapes = -> [Box097,Fusion069]
FEATURE [Part::MultiFuse] Fusion071
  Shapes = -> [Fusion070,Box098]
FEATURE [Part::Cut] Cut103
  Base = -> Fusion071
  Tool = -> Cylinder076
FEATURE [Part::Cut] Cut104  label="Servo002"
  Base = -> Cut103
  Tool = -> Cylinder077
FEATURE [Part::MultiFuse] Fusion072
  Shapes = -> [Cylinder078,Box099]
FEATURE [Part::Fillet] Fillet036
  Base = -> Fusion072
  Edges = 1 edges r=2: [Edge4]
FEATURE [Part::Fillet] Fillet037
  Base = -> Fillet036
  Edges = 1 edges r=1: [Edge25]
FEATURE [Part::Fillet] Fillet038
  Base = -> Fillet037
  Edges = 1 edges r=1: [Edge17]
FEATURE [Part::MultiFuse] Fusion073
  Shapes = -> [Cut104,Fillet038]
FEATURE [Part::Cut] Cut105
  Base = -> Fusion073
  Tool = -> Cylinder079
FEATURE [Part::Cut] Cut106
  Base = -> Cut105
  Tool = -> Cylinder083
FEATURE [Part::Cut] Cut107
  Base = -> Cut106
  Tool = -> Cylinder082
FEATURE [Part::Cut] Cut108
  Base = -> Cut107
  Tool = -> Cylinder081
FEATURE [Part::Cut] Cut109  label="Servo003"
  Base = -> Cut108
  Placement = pos=(41,12,85) rot=(0.707107,-0.707107,0;3.14159rad)
  Tool = -> Cylinder080
FEATURE [Part::Cut] Cut110
  Base = -> Cut102
  Tool = -> Cut109
FEATURE [Part::MultiFuse] Fusion
  Shapes = -> [Cut110,Fillet041]
FEATURE [Part::MultiFuse] Fusion074  label="Lateral_De002"
  Shapes = -> [Fusion,Fillet042]
FEATURE [Part::MultiFuse] Fusion078
  Shapes = -> [Cylinder092,Cylinder093]
FEATURE [Part::MultiFuse] Fusion079
  Shapes = -> [Box115,Fusion078]
FEATURE [Part::MultiFuse] Fusion080
  Shapes = -> [Fusion079,Box116]
FEATURE [Part::Cut] Cut127
  Base = -> Fusion080
  Tool = -> Cylinder094
FEATURE [Part::Cut] Cut128  label="Servo004"
  Base = -> Cut127
  Tool = -> Cylinder095
FEATURE [Part::MultiFuse] Fusion081
  Shapes = -> [Cylinder096,Box117]
FEATURE [Part::Fillet] Fillet055
  Base = -> Fusion081
  Edges = 1 edges r=2: [Edge4]
FEATURE [Part::Fillet] Fillet056
  Base = -> Fillet055
  Edges = 1 edges r=1: [Edge25]
FEATURE [Part::Fillet] Fillet057
  Base = -> Fillet056
  Edges = 1 edges r=1: [Edge17]
FEATURE [Part::MultiFuse] Fusion082
  Shapes = -> [Cut128,Fillet057]
FEATURE [Part::Cut] Cut129
  Base = -> Fusion082
  Tool = -> Cylinder097
FEATURE [Part::Cut] Cut130
  Base = -> Cut129
  Tool = -> Cylinder101
FEATURE [Part::Cut] Cut131
  Base = -> Cut130
  Tool = -> Cylinder100
FEATURE [Part::Cut] Cut132
  Base = -> Cut131
  Tool = -> Cylinder099
FEATURE [Part::Cut] Cut133  label="Servo005"
  Base = -> Cut132
  Placement = pos=(41,12,85) rot=(0.707107,-0.707107,0;3.14159rad)
  Tool = -> Cylinder098
FEATURE [Part::Cut] Cut134
  Base = -> Cut126
  Tool = -> Cut133
FEATURE [Part::MultiFuse] Fusion077
  Shapes = -> [Cut134,Fillet060]
FEATURE [Part::MultiFuse] Fusion083  label="Lateral_De006"
  Shapes = -> [Fusion077,Fillet061]
FEATURE [Part::MultiFuse] Fusion084
  Shapes = -> [Fillet073,Box130]
FEATURE [Part::Fillet] Fillet077
  Base = -> Fusion084
  Edges = 2 edges r=1: [Edge2,Edge16]
FEATURE [Part::Fillet] Fillet078  label="PortaSensor_TemHum002"
  Base = -> Fillet077
  Edges = 2 edges r=1: [Edge20,Edge56]
FEATURE [Part::Fillet] Fillet079
  Base = -> Fillet078
  Edges = 1 edges r=1.5: [Edge45]
FEATURE [Part::Fillet] Fillet080  label="PortaSensor_TemHum003"
  Base = -> Fillet079
  Edges = 1 edges r=1.5: [Edge39]
  Placement = pos=(1,15.5,0) rot=(0,0,1;0rad)
FEATURE [Part::MultiFuse] Fusion097
  Shapes = -> [Cylinder144,Cylinder145]
FEATURE [Part::MultiFuse] Fusion098
  Shapes = -> [Box177,Fusion097]
FEATURE [Part::MultiFuse] Fusion099
  Shapes = -> [Fusion098,Box178]
FEATURE [Part::Cut] Cut218
  Base = -> Fusion099
  Tool = -> Cylinder146
FEATURE [Part::Cut] Cut219  label="Servo006"
  Base = -> Cut218
  Tool = -> Cylinder147
FEATURE [Part::MultiFuse] Fusion100
  Shapes = -> [Cylinder148,Box179]
FEATURE [Part::Fillet] Fillet127
  Base = -> Fusion100
  Edges = 1 edges r=2: [Edge4]
FEATURE [Part::Fillet] Fillet128
  Base = -> Fillet127
  Edges = 1 edges r=1: [Edge25]
FEATURE [Part::Fillet] Fillet129
  Base = -> Fillet128
  Edges = 1 edges r=1: [Edge17]
FEATURE [Part::MultiFuse] Fusion101
  Shapes = -> [Cut219,Fillet129]
FEATURE [Part::Cut] Cut220
  Base = -> Fusion101
  Tool = -> Cylinder149
FEATURE [Part::Cut] Cut221
  Base = -> Cut220
  Tool = -> Cylinder153
FEATURE [Part::Cut] Cut222
  Base = -> Cut221
  Tool = -> Cylinder152
FEATURE [Part::Cut] Cut223
  Base = -> Cut222
  Tool = -> Cylinder151
FEATURE [Part::Cut] Cut224  label="Servo007"
  Base = -> Cut223
  Placement = pos=(41,12,85) rot=(0.707107,-0.707107,0;3.14159rad)
  Tool = -> Cylinder150
FEATURE [Part::Cut] Cut225
  Base = -> Cut217
  Tool = -> Cut224
FEATURE [Part::MultiFuse] Fusion096
  Shapes = -> [Cut225,Fillet132]
FEATURE [Part::MultiFuse] Fusion102  label="Lateral_De010"
  Shapes = -> [Fusion096,Fillet133]
FEATURE [Part::Offset] Offset
  Fill = false
  Intersection = false
  Join = 0
  Mode = 0
  SelfIntersection = false
  Source = -> Fillet011
  Value = 0.2
FEATURE [Part::Cut] Cut004
  Base = -> Cut003
  Tool = -> Offset
FEATURE [Part::Offset] Offset001
  Fill = false
  Intersection = false
  Join = 0
  Mode = 0
  SelfIntersection = false
  Source = -> Fillet013
  Value = 0.2
FEATURE [Part::Cut] Cut005  label="Base_2"
  Base = -> Cut004
  Placement = pos=(0,0,10) rot=(0,0,1;0rad)
  Tool = -> Offset001
FEATURE [Part::Cut] Cut012
  Base = -> Cut005
  Tool = -> Fillet019
FEATURE [Part::Cut] Cut013
  Base = -> Cut012
  Tool = -> Fillet022
FEATURE [Part::MultiFuse] Fusion002  label="BaseSup"
  Shapes = -> [Cut013,Cut017]
FEATURE [Part::MultiFuse] Fusion075  label="BaseSup001"
  Shapes = -> [Fusion002,Fillet046]
FEATURE [Part::Fillet] Fillet047
  Base = -> Fusion075
  Edges = 1 edges r=2: [Edge125]
FEATURE [Part::Fillet] Fillet048
  Base = -> Fillet047
  Edges = 1 edges r=2: [Edge136]
FEATURE [Part::MultiFuse] Fusion076
  Shapes = -> [Fillet048,Fillet007]
FEATURE [Part::Chamfer] Chamfer  label="BaseSup002"
  Base = -> Fusion076
  Edges = 1 edges r=2: [Edge137]
FEATURE [Part::Cut] Cut119
  Base = -> Chamfer
  Tool = -> Fillet049
FEATURE [Part::Fillet] Fillet050  label="BaseSup003"
  Base = -> Cut119
  Edges = 2 edges r=1: [Edge41,Edge45]
FEATURE [Part::Cut] Cut147  label="BaseInf007"
  Base = -> Fillet050
  Tool = -> Box128
FEATURE [Part::Cut] Cut148
  Base = -> Cut147
  Tool = -> Box129
FEATURE [Part::Cut] Cut151  label="BaseSup004"
  Base = -> Cut148
  Tool = -> Box134
FEATURE [Part::MultiFuse] Fusion085
  Shapes = -> [Cut151,Fillet084]
FEATURE [Part::MultiFuse] Fusion086
  Shapes = -> [Fusion085,Fillet082]
FEATURE [Part::MultiFuse] Fusion087  label="BaseSup005"
  Shapes = -> [Fusion086,Fillet080]
FEATURE [Part::Cut] Cut235
  Base = -> Fusion087
  Tool = -> Box184
FEATURE [Part::Fillet] Fillet141
  Base = -> Cut235
  Edges = 1 edges r=2.5: [Edge15]
FEATURE [Part::Fillet] Fillet142
  Base = -> Fillet141
  Edges = 1 edges r=2.5: [Edge97]
FEATURE [Part::Fillet] Fillet143
  Base = -> Fillet142
  Edges = 1 edges r=2.5: [Edge20]
FEATURE [Part::Fillet] Fillet144  label="BloquComponentes"
  Base = -> Fillet143
  Edges = 1 edges r=2.5: [Edge92]
FEATURE [Part::MultiFuse] Fusion103
  Shapes = -> [Fillet144,Cylinder158]
FEATURE [Part::MultiFuse] Fusion104
  Shapes = -> [Fusion103,Cylinder161]
FEATURE [Part::MultiFuse] Fusion105
  Shapes = -> [Fusion104,Cylinder160]
FEATURE [Part::MultiFuse] Fusion106
  Shapes = -> [Fusion105,Cylinder159]
FEATURE [Part::MultiFuse] Fusion107
  Shapes = -> [Fusion106,Fillet146]
FEATURE [Part::MultiFuse] Fusion108
  Shapes = -> [Fusion107,Fillet148]
FEATURE [Part::Offset] Offset002
  Fill = false
  Intersection = false
  Join = 0
  Mode = 0
  SelfIntersection = false
  Source = -> Box
  Value = 0.2
FEATURE [Part::Cut] Cut114  label="Lateral_De003"
  Base = -> Fusion074
  Tool = -> Offset002
FEATURE [Part::Cut] Cut177
  Base = -> Cut114
  Tool = -> Box165
FEATURE [Part::Cut] Cut179
  Base = -> Cut177
  Tool = -> Box167
FEATURE [Part::Cut] Cut181
  Base = -> Cut179
  Tool = -> Cylinder110
FEATURE [Part::Cut] Cut182
  Base = -> Cut181
  Tool = -> Cylinder111
FEATURE [Part::Cut] Cut183
  Base = -> Cut182
  Tool = -> Cylinder112
FEATURE [Part::Cut] Cut184
  Base = -> Cut183
  Tool = -> Cylinder120
FEATURE [Part::Cut] Cut185
  Base = -> Cut184
  Tool = -> Cylinder119
FEATURE [Part::Cut] Cut186
  Base = -> Cut185
  Tool = -> Cylinder118
FEATURE [Part::Cut] Cut187
  Base = -> Cut186
  Tool = -> Cylinder117
FEATURE [Part::Cut] Cut188
  Base = -> Cut187
  Tool = -> Cylinder116
FEATURE [Part::Cut] Cut189
  Base = -> Cut188
  Tool = -> Cylinder115
FEATURE [Part::Cut] Cut190
  Base = -> Cut189
  Tool = -> Cylinder114
FEATURE [Part::Cut] Cut191  label="LateralDer"
  Base = -> Cut190
  Tool = -> Cylinder113
FEATURE [Part::Cut] Cut202
  Base = -> Cut191
  Tool = -> Box168
FEATURE [Part::Cut] Cut203  label="LateralDer001"
  Base = -> Cut202
  Tool = -> Box169
FEATURE [Part::Cut] Cut255  label="LateralDer002"
  Base = -> Cut203
  Tool = -> Box197
FEATURE [Part::Cut] Cut256  label="LateralDer003"
  Base = -> Cut255
  Tool = -> Box198
FEATURE [Part::Offset] Offset003
  Fill = false
  Intersection = false
  Join = 0
  Mode = 0
  SelfIntersection = false
  Source = -> Box102
  Value = 0.2
FEATURE [Part::Cut] Cut113  label="Lateral_Iz003"
  Base = -> Cut099
  Tool = -> Offset003
FEATURE [Part::Cut] Cut178
  Base = -> Cut113
  Tool = -> Box166
FEATURE [Part::Cut] Cut180
  Base = -> Cut178
  Tool = -> Cylinder109
FEATURE [Part::Cut] Cut192
  Base = -> Cut180
  Tool = -> Cylinder121
FEATURE [Part::Cut] Cut193
  Base = -> Cut192
  Tool = -> Cylinder130
FEATURE [Part::Cut] Cut194
  Base = -> Cut193
  Tool = -> Cylinder129
FEATURE [Part::MultiFuse] Fusion095
  Shapes = -> [Cut194,Cylinder128]
FEATURE [Part::Cut] Cut195
  Base = -> Fusion095
  Tool = -> Cylinder127
FEATURE [Part::Cut] Cut196
  Base = -> Cut195
  Tool = -> Cylinder126
FEATURE [Part::Cut] Cut197
  Base = -> Cut196
  Tool = -> Cylinder125
FEATURE [Part::Cut] Cut198
  Base = -> Cut197
  Tool = -> Cylinder124
FEATURE [Part::Cut] Cut199
  Base = -> Cut198
  Tool = -> Cylinder123
FEATURE [Part::Cut] Cut200
  Base = -> Cut199
  Tool = -> Cylinder122
FEATURE [Part::Cut] Cut201  label="LateralIzq"
  Base = -> Cut200
  Tool = -> Cylinder131
FEATURE [Part::Offset] Offset004
  Fill = false
  Intersection = false
  Join = 0
  Mode = 0
  SelfIntersection = false
  Source = -> Box112
  Value = 0.2
FEATURE [Part::Cut] Cut123  label="Lateral_Iz005"
  Base = -> Cut122
  Tool = -> Offset004
FEATURE [Part::Cut] Cut138
  Base = -> Cut096
  Tool = -> Cut123
FEATURE [Part::Offset] Offset005
  Fill = false
  Intersection = false
  Join = 0
  Mode = 0
  SelfIntersection = false
  Source = -> Box113
  Value = 0.2
FEATURE [Part::Cut] Cut137  label="Lateral_De004"
  Base = -> Fusion083
  Tool = -> Offset005
FEATURE [Part::Cut] Cut139  label="BaseInf004"
  Base = -> Cut138
  Tool = -> Cut137
FEATURE [Part::Offset] Offset006
  Fill = false
  Intersection = false
  Join = 0
  Mode = 0
  SelfIntersection = false
  Source = -> Fillet063
  Value = 0.2
FEATURE [Part::Cut] Cut140
  Base = -> Cut139
  Tool = -> Offset006
FEATURE [Part::Offset] Offset007
  Fill = false
  Intersection = false
  Join = 0
  Mode = 0
  Placement = pos=(56,0,0) rot=(0,0,1;0rad)
  SelfIntersection = false
  Source = -> Fillet065
  Value = 0.2
FEATURE [Part::Cut] Cut141
  Base = -> Cut140
  Tool = -> Offset007
FEATURE [Part::Fillet] Fillet066
  Base = -> Cut141
  Edges = 7 edges r=1: [Edge55,Edge56,Edge57,Edge58,Edge59,Edge60,Edge61]
FEATURE [Part::Fillet] Fillet067
  Base = -> Fillet066
  Edges = 2 edges r=1: [Edge34,Edge38]
FEATURE [Part::Fillet] Fillet068  label="BaseInf005"
  Base = -> Fillet067
  Edges = 2 edges r=1: [Edge28,Edge32]
FEATURE [Part::Cut] Cut142  label="BaseInf006"
  Base = -> Fillet068
  Tool = -> Cylinder104
FEATURE [Part::Cut] Cut204  label="BaseInf009"
  Base = -> Cut142
  Tool = -> Cylinder133
FEATURE [Part::Offset] Offset010
  Fill = false
  Intersection = false
  Join = 0
  Mode = 0
  SelfIntersection = false
  Source = -> Box174
  Value = 0.2
FEATURE [Part::Cut] Cut214  label="Lateral_Iz009"
  Base = -> Cut213
  Tool = -> Offset010
FEATURE [Part::Cut] Cut229
  Base = -> Cut210
  Tool = -> Cut214
FEATURE [Part::Offset] Offset011
  Fill = false
  Intersection = false
  Join = 0
  Mode = 0
  SelfIntersection = false
  Source = -> Box175
  Value = 0.2
FEATURE [Part::Cut] Cut228  label="Lateral_De008"
  Base = -> Fusion102
  Tool = -> Offset011
FEATURE [Part::Cut] Cut230  label="BaseInf014"
  Base = -> Cut229
  Tool = -> Cut228
FEATURE [Part::Offset] Offset012
  Fill = false
  Intersection = false
  Join = 0
  Mode = 0
  SelfIntersection = false
  Source = -> Fillet135
  Value = 0.2
FEATURE [Part::Cut] Cut231
  Base = -> Cut230
  Tool = -> Offset012
FEATURE [Part::Offset] Offset013
  Fill = false
  Intersection = false
  Join = 0
  Mode = 0
  Placement = pos=(56,0,0) rot=(0,0,1;0rad)
  SelfIntersection = false
  Source = -> Fillet137
  Value = 0.2
FEATURE [Part::Cut] Cut232
  Base = -> Cut231
  Tool = -> Offset013
FEATURE [Part::Fillet] Fillet138
  Base = -> Cut232
  Edges = 7 edges r=1: [Edge55,Edge56,Edge57,Edge58,Edge59,Edge60,Edge61]
FEATURE [Part::Fillet] Fillet139
  Base = -> Fillet138
  Edges = 2 edges r=1: [Edge34,Edge38]
FEATURE [Part::Fillet] Fillet140  label="BaseInf017"
  Base = -> Fillet139
  Edges = 2 edges r=1: [Edge28,Edge32]
FEATURE [Part::Cut] Cut233  label="BaseInf015"
  Base = -> Fillet140
  Tool = -> Cylinder156
FEATURE [Part::Cut] Cut234  label="BaseSup012"
  Base = -> Cut233
  Placement = pos=(0,0,105) rot=(0,0,1;0rad)
  Tool = -> Cylinder157
FEATURE [Part::MultiFuse] Fusion109  label="BaseSup013"
  Shapes = -> [Cut234,Fusion108]
FEATURE [Part::MultiFuse] Fusion178  label="Capsula_Paracaidas"
  Shapes = -> [Cut201,Cut204,Fusion109,Cut256]
